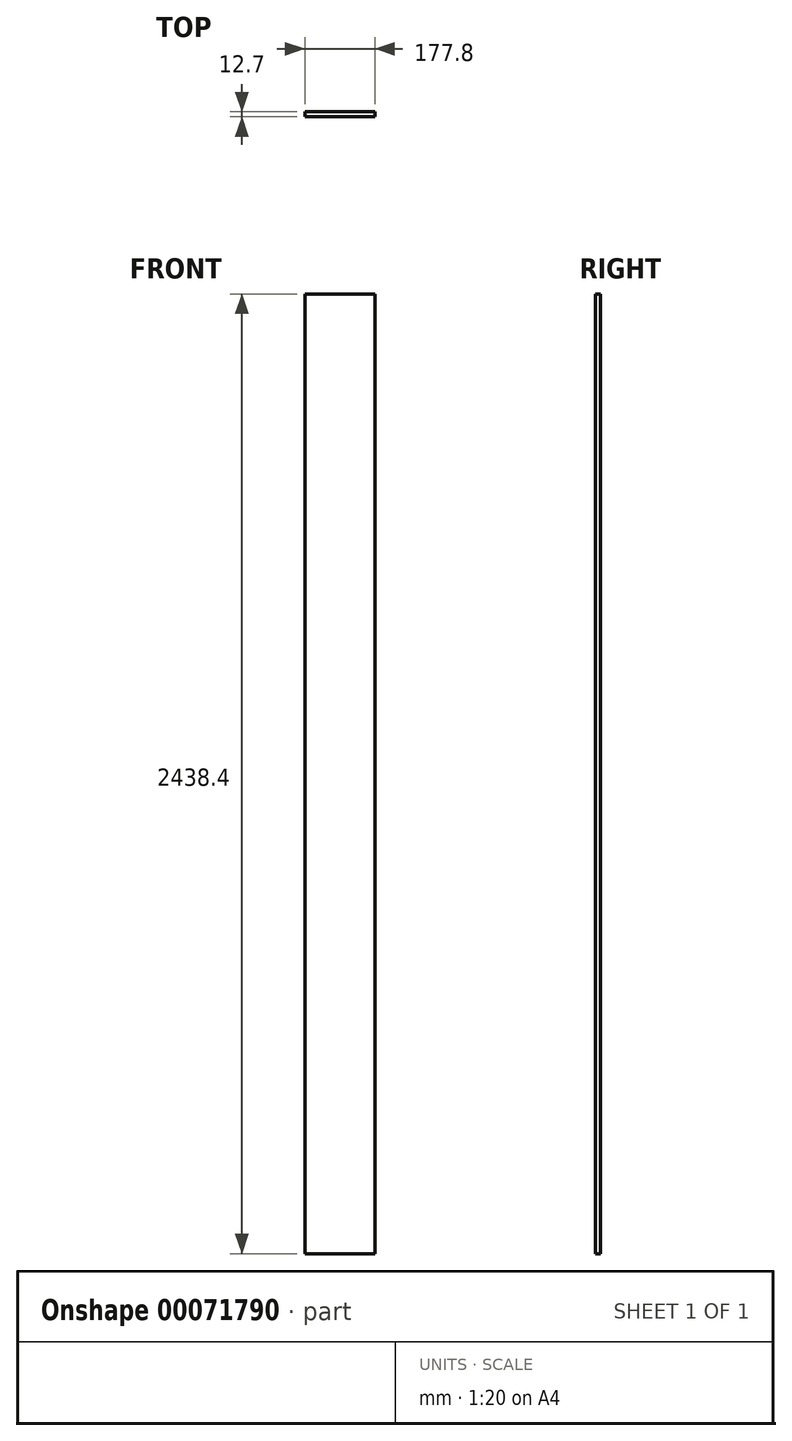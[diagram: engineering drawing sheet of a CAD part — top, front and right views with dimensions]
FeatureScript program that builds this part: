
annotation { "Feature Type Name" : "Feature", "Feature Type Description" : "" }
export const myFeature = defineFeature(function(context is Context, id is Id, definition is map)
    precondition{}
    {
        {
            var Q0;
            Q0=qCreatedBy(makeId("Front.planeOp"),FACE);
            var sketch = newSketch(context, id + "F0", { "sketchPlane" : qUnion([Q0])});
            skLineSegment(sketch, "E0.rect.bottom", {"start": v(88.9, -1219.2) * mm, "end": v(-88.9, -1219.2) * mm});
            skLineSegment(sketch, "E0.rect.top", {"start": v(88.9, 1219.2) * mm, "end": v(-88.9, 1219.2) * mm});
            skLineSegment(sketch, "E0.rect.left", {"start": v(88.9, -1219.2) * mm, "end": v(88.9, 1219.2) * mm});
            skLineSegment(sketch, "E0.rect.right", {"start": v(-88.9, -1219.2) * mm, "end": v(-88.9, 1219.2) * mm});
            skPoint(sketch, "E0.rect.middle", {"position": v(0, 0) * mm});
            skSolve(sketch);
        }
        {
            var Q0;
            Q0 = qSketchRegion(id + "F0", true);
            extrude(context, id + "F1", {"entities" : qUnion([Q0]), "oppositeDirection" : true, "depth" : 12.7 * mm});
        }
    });
